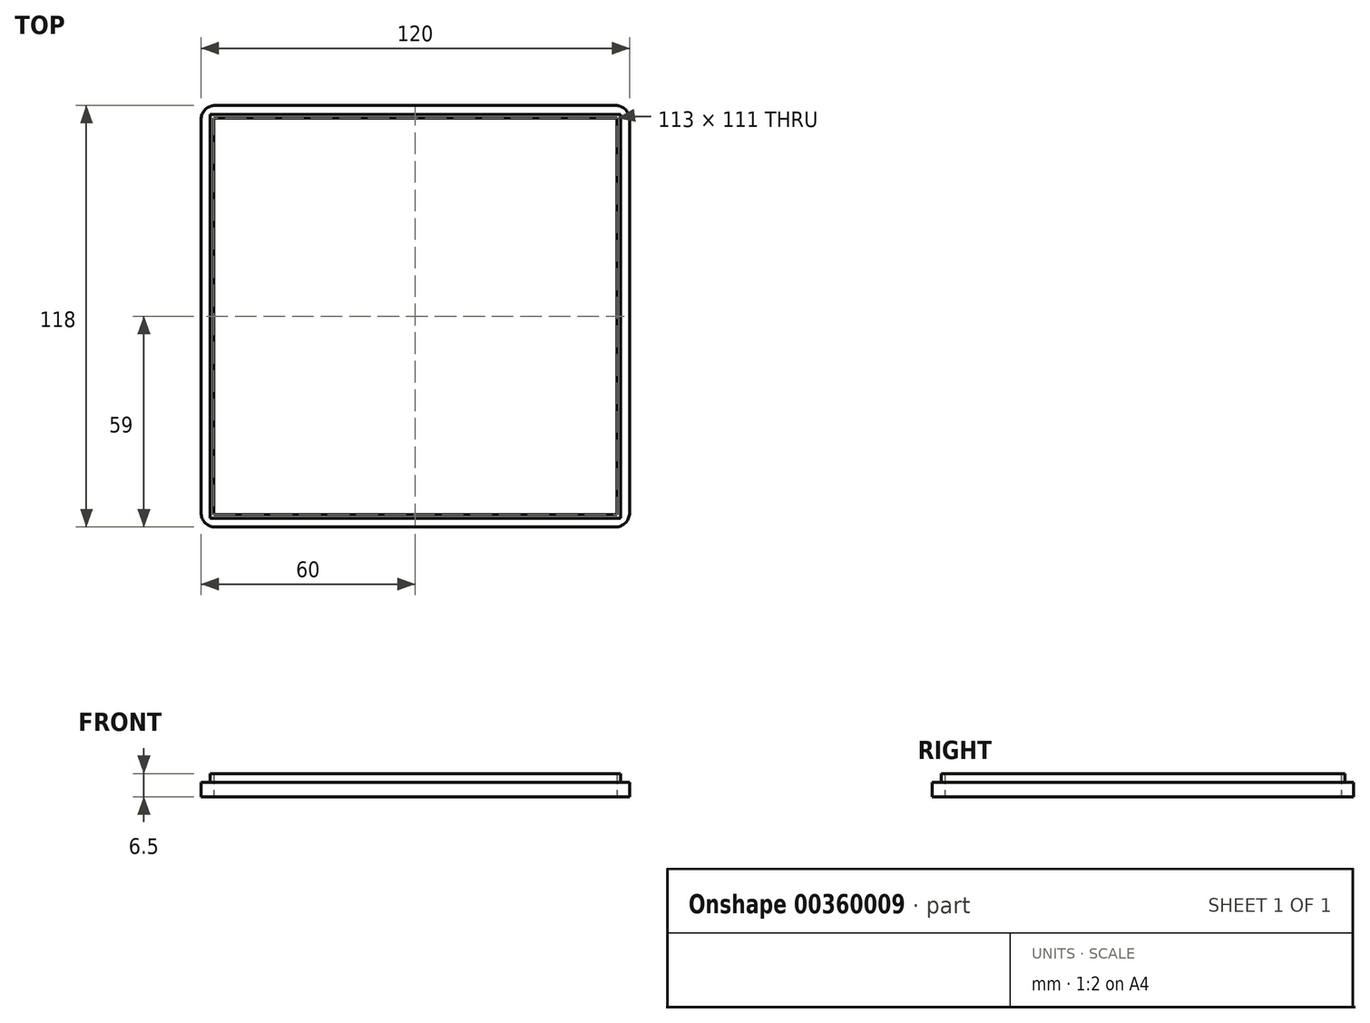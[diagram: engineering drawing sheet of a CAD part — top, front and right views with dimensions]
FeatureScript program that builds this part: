
annotation { "Feature Type Name" : "Feature", "Feature Type Description" : "" }
export const myFeature = defineFeature(function(context is Context, id is Id, definition is map)
    precondition{}
    {
        {
            var Q0;
            Q0=qCreatedBy(makeId("Top.planeOp"),FACE);
            var sketch = newSketch(context, id + "F0", { "sketchPlane" : qUnion([Q0])});
            skLineSegment(sketch, "E0.bottom", {"start": v(-60, 59) * mm, "end": v(60, 59) * mm});
            skLineSegment(sketch, "E0.top", {"start": v(-60, -59) * mm, "end": v(60, -59) * mm});
            skLineSegment(sketch, "E0.left", {"start": v(-60, 59) * mm, "end": v(-60, -59) * mm});
            skLineSegment(sketch, "E0.right", {"start": v(60, 59) * mm, "end": v(60, -59) * mm});
            skPoint(sketch, "E0.middle", {"position": v(0, 0) * mm});
            skSolve(sketch);
        }
        {
            var Q0;
            Q0 = qSketchRegion(id + "F0", true);
            extrude(context, id + "F1", {"entities" : qUnion([Q0]), "depth" : 4 * mm});
        }
        {
            var Q0;
            Q0=makeQuery(id+"F1.opExtrude","CAP_FACE",FACE,{"disambiguationData":[OSD([sQuery(id+"F0.wireOp",EDGE,"E0.bottom"),sQuery(id+"F0.wireOp",EDGE,"E0.top"),sQuery(id+"F0.wireOp",EDGE,"E0.left"),sQuery(id+"F0.wireOp",EDGE,"E0.right")])],"isStart":false});
            var sketch = newSketch(context, id + "F2", { "sketchPlane" : qUnion([Q0])});
            skLineSegment(sketch, "E1.bottom", {"start": v(-57.5, 56.5) * mm, "end": v(-56.5, 56.5) * mm});
            skLineSegment(sketch, "E1.top", {"start": v(-57.5, -56.5) * mm, "end": v(-56.5, -56.5) * mm});
            skLineSegment(sketch, "E1.left", {"start": v(-57.5, 56.5) * mm, "end": v(-57.5, -56.5) * mm});
            skLineSegment(sketch, "E1.right", {"start": v(-56.5, 56.5) * mm, "end": v(-56.5, -56.5) * mm});
            skLineSegment(sketch, "E2.bottom", {"start": v(-57.5, -56.5) * mm, "end": v(57.5, -56.5) * mm});
            skLineSegment(sketch, "E2.top", {"start": v(-57.5, -55.5) * mm, "end": v(57.5, -55.5) * mm});
            skLineSegment(sketch, "E2.left", {"start": v(-57.5, -56.5) * mm, "end": v(-57.5, -55.5) * mm});
            skLineSegment(sketch, "E2.right", {"start": v(57.5, -56.5) * mm, "end": v(57.5, -55.5) * mm});
            skLineSegment(sketch, "E3.bottom", {"start": v(57.5, -56.5) * mm, "end": v(56.5, -56.5) * mm});
            skLineSegment(sketch, "E3.top", {"start": v(57.5, 56.5) * mm, "end": v(56.5, 56.5) * mm});
            skLineSegment(sketch, "E3.left", {"start": v(57.5, -56.5) * mm, "end": v(57.5, 56.5) * mm});
            skLineSegment(sketch, "E3.right", {"start": v(56.5, -56.5) * mm, "end": v(56.5, 56.5) * mm});
            skLineSegment(sketch, "E4.bottom", {"start": v(57.5, 56.5) * mm, "end": v(-57.5, 56.5) * mm});
            skLineSegment(sketch, "E4.top", {"start": v(57.5, 55.5) * mm, "end": v(-57.5, 55.5) * mm});
            skLineSegment(sketch, "E4.left", {"start": v(57.5, 56.5) * mm, "end": v(57.5, 55.5) * mm});
            skLineSegment(sketch, "E4.right", {"start": v(-57.5, 56.5) * mm, "end": v(-57.5, 55.5) * mm});
            skSolve(sketch);
        }
        {
            var Q0;
            Q0 = qSketchRegion(id + "F2", true);
            extrude(context, id + "F3", {"entities" : qUnion([Q0]), "operationType" : NewBodyOperationType.ADD, "depth" : 2.5 * mm});
        }
        {
            var Q0;
            {var subQ0=sQuery(id+"F2.wireOp",EDGE,"E4.top");var subQ1=sQuery(id+"F2.wireOp",EDGE,"E1.right");var subQ2=makeQuery(id+"F2.imprint","INTERSECT",VERTEX,{"derivedFrom":[subQ1,subQ0]});Q0=makeQuery(id+"F2.imprint","IMPRINT",FACE,{"disambiguationData":[TD([[makeQuery(id+"F2.imprint","IMPRINT",EDGE,{"disambiguationData":[TD([[subQ2,-1.0]])],"derivedFrom":subQ1}),1.0]])]});}
            var sketch = newSketch(context, id + "F4", { "sketchPlane" : qUnion([Q0])});
            skLineSegment(sketch, "E5.bottom", {"start": v(-56.5, 55.5) * mm, "end": v(56.5, 55.5) * mm});
            skLineSegment(sketch, "E5.top", {"start": v(-56.5, -55.5) * mm, "end": v(56.5, -55.5) * mm});
            skLineSegment(sketch, "E5.left", {"start": v(-56.5, 55.5) * mm, "end": v(-56.5, -55.5) * mm});
            skLineSegment(sketch, "E5.right", {"start": v(56.5, 55.5) * mm, "end": v(56.5, -55.5) * mm});
            skPoint(sketch, "E5.middle", {"position": v(0, 0) * mm});
            skSolve(sketch);
        }
        {
            var Q0;
            Q0 = qSketchRegion(id + "F4", true);
            extrude(context, id + "F5", {"entities" : qUnion([Q0]), "operationType" : NewBodyOperationType.REMOVE, "oppositeDirection" : true, "depth" : 5 * mm});
        }
        {
            var Q0;
            Q0=makeQuery(id+"F1.opExtrude","SWEPT_EDGE",EDGE,{"disambiguationData":[OSD([sQuery(id+"F0.wireOp",EDGE,"E0.bottom"),sQuery(id+"F0.wireOp",EDGE,"E0.left")])]});
            var Q1;
            Q1=makeQuery(id+"F1.opExtrude","SWEPT_EDGE",EDGE,{"disambiguationData":[OSD([sQuery(id+"F0.wireOp",EDGE,"E0.bottom"),sQuery(id+"F0.wireOp",EDGE,"E0.right")])]});
            var Q2;
            Q2=makeQuery(id+"F1.opExtrude","SWEPT_EDGE",EDGE,{"disambiguationData":[OSD([sQuery(id+"F0.wireOp",EDGE,"E0.top"),sQuery(id+"F0.wireOp",EDGE,"E0.right")])]});
            var Q3;
            Q3=makeQuery(id+"F1.opExtrude","SWEPT_EDGE",EDGE,{"disambiguationData":[OSD([sQuery(id+"F0.wireOp",EDGE,"E0.top"),sQuery(id+"F0.wireOp",EDGE,"E0.left")])]});
            fillet(context, id + "F6", {"entities" : qUnion([Q0, Q1, Q2, Q3]), "radius" : 4 * mm, "tangentPropagation" : true, "allowEdgeOverflow" : false});
        }
    });
